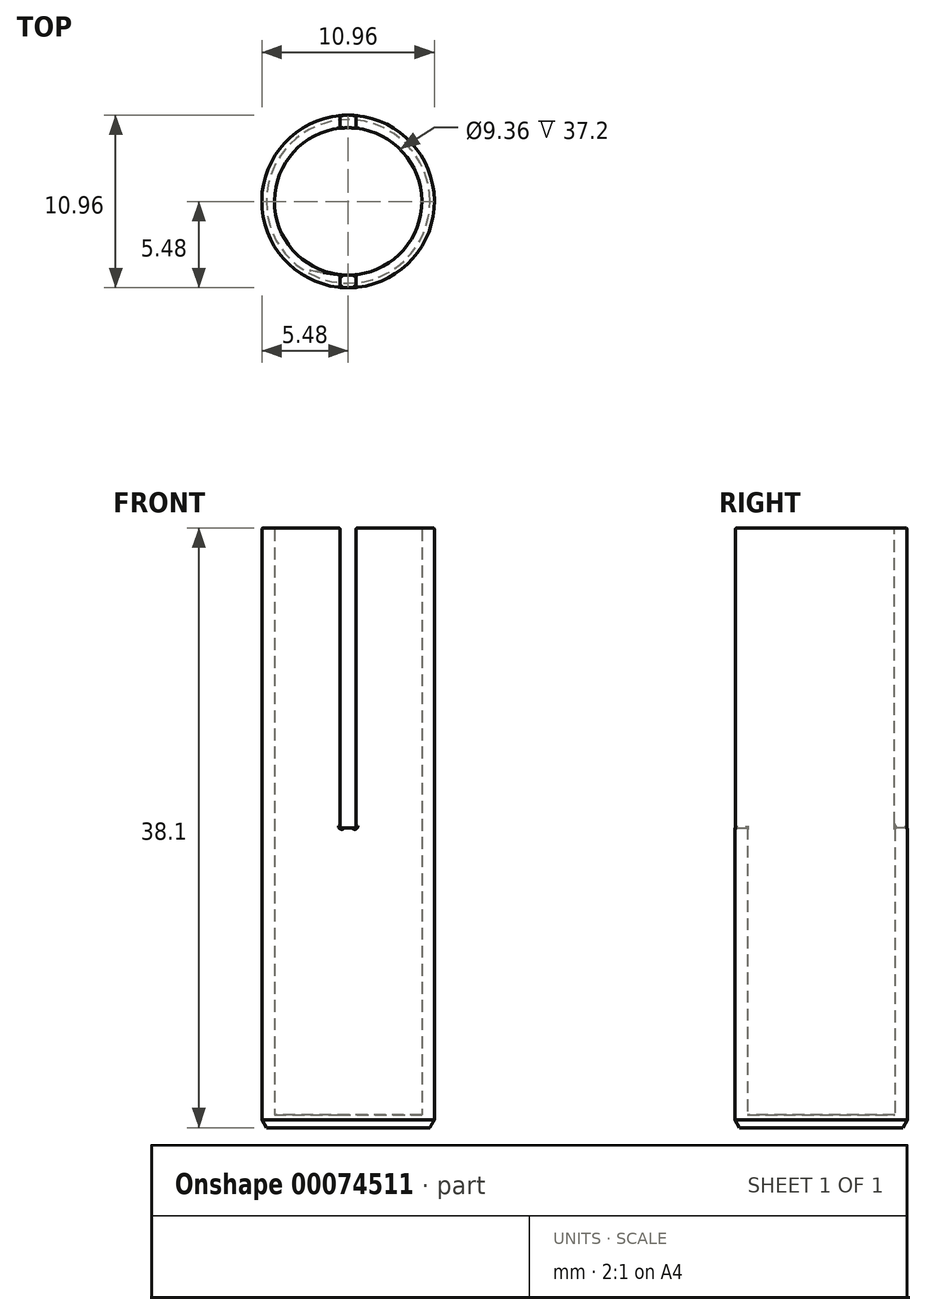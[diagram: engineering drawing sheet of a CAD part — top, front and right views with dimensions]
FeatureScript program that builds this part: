
annotation { "Feature Type Name" : "Feature", "Feature Type Description" : "" }
export const myFeature = defineFeature(function(context is Context, id is Id, definition is map)
    precondition{}
    {
        {
            var Q0;
            Q0=qCreatedBy(makeId("Top.planeOp"),FACE);
            var sketch = newSketch(context, id + "F0", { "sketchPlane" : qUnion([Q0])});
            skCircle(sketch, "E0", {"center": v(0, 0) * mm, "radius": 5.48 * mm});
            skCircle(sketch, "E1", {"center": v(0, 0) * mm, "radius": 5.08 * mm, "construction": true});
            skSolve(sketch);
        }
        {
            var Q0;
            Q0=makeQuery(id+"F0.imprint","IMPRINT",FACE,{"disambiguationData":[TD([[makeQuery(id+"F0.imprint","IMPRINT",EDGE,{"derivedFrom":sQuery(id+"F0.wireOp",EDGE,"E0")}),1.0]])]});
            extrude(context, id + "F1", {"entities" : qUnion([Q0]), "depth" : 38.1 * mm});
        }
        {
            var Q0;
            Q0=makeQuery(id+"F1.opExtrude","CAP_FACE",FACE,{"disambiguationData":[OSD([sQuery(id+"F0.wireOp",EDGE,"E0")])],"isStart":false});
            shell(context, id + "F2", {"entities" : qUnion([Q0]), "thickness" : 0.8 * mm});
        }
        {
            var Q0;
            Q0=makeQuery(id+"F1.opExtrude","CAP_FACE",FACE,{"disambiguationData":[OSD([sQuery(id+"F0.wireOp",EDGE,"E0")])],"isStart":false});
            var sketch = newSketch(context, id + "F3", { "sketchPlane" : qUnion([Q0])});
            skLineSegment(sketch, "E2", {"start": v(0, 5.48) * mm, "end": v(0, 4.68) * mm, "construction": true});
            skLineSegment(sketch, "E3", {"start": v(0.5, 5.46) * mm, "end": v(0.5, 4.65) * mm});
            skLineSegment(sketch, "E4.MirrorCS", {"start": v(-0.5, 5.46) * mm, "end": v(-0.5, 4.65) * mm});
            skArc(sketch, "E5.0", {"start": v(0.5, 4.65) * mm, "mid": v(0, 4.68) * mm, "end": v(-0.5, 4.65) * mm});
            skArc(sketch, "E6.0", {"start": v(0.5, 5.46) * mm, "mid": v(0, 5.48) * mm, "end": v(-0.5, 5.46) * mm});
            skLineSegment(sketch, "E7", {"start": v(0, 4.68) * mm, "end": v(0, -4.68) * mm, "construction": true});
            skLineSegment(sketch, "E8", {"start": v(0, 0) * mm, "end": v(-4.68, 0) * mm, "construction": true});
            skArc(sketch, "E9.MirrorCS", {"start": v(0.5, -4.65) * mm, "mid": v(0, -4.68) * mm, "end": v(-0.5, -4.65) * mm});
            skLineSegment(sketch, "E10.MirrorCS", {"start": v(0.5, -5.46) * mm, "end": v(0.5, -4.65) * mm});
            skArc(sketch, "E11.MirrorCS", {"start": v(0.5, -5.46) * mm, "mid": v(0, -5.48) * mm, "end": v(-0.5, -5.46) * mm});
            skLineSegment(sketch, "E12.MirrorCS", {"start": v(-0.5, -5.46) * mm, "end": v(-0.5, -4.65) * mm});
            skSolve(sketch);
        }
        {
            var Q0;
            Q0 = qSketchRegion(id + "F3", true);
            extrude(context, id + "F4", {"entities" : qUnion([Q0]), "operationType" : NewBodyOperationType.REMOVE, "oppositeDirection" : true, "depth" : 19.05 * mm});
        }
        {
            var Q0;
            {var subQ0=sQuery(id+"F0.wireOp",EDGE,"E0");Q0=makeQuery(id+"F4.boolean.opBoolean","SPLIT",FACE,{"disambiguationData":[TD([makeQuery(id+"F4.opExtrude","SWEPT_FACE",FACE,{"disambiguationData":[OSD([sQuery(id+"F3.wireOp",EDGE,"E4.MirrorCS")])]})])],"derivedFrom":makeQuery(id+"F1.opExtrude","CAP_FACE",FACE,{"disambiguationData":[OSD([subQ0])],"isStart":false})});}
            var Q1;
            {var subQ0=sQuery(id+"F0.wireOp",EDGE,"E0");Q1=makeQuery(id+"F4.boolean.opBoolean","SPLIT",FACE,{"disambiguationData":[TD([makeQuery(id+"F4.opExtrude","SWEPT_FACE",FACE,{"disambiguationData":[OSD([sQuery(id+"F3.wireOp",EDGE,"E3")])]})])],"derivedFrom":makeQuery(id+"F1.opExtrude","CAP_FACE",FACE,{"disambiguationData":[OSD([subQ0])],"isStart":false})});}
            var Q2;
            Q2=makeQuery(id+"F4.boolean.opBoolean","COPY",FACE,{"derivedFrom":makeQuery(id+"F4.opExtrude","SWEPT_FACE",FACE,{"disambiguationData":[OSD([sQuery(id+"F3.wireOp",EDGE,"E10.MirrorCS")])]})});
            var Q3;
            Q3=makeQuery(id+"F4.boolean.opBoolean","COPY",FACE,{"derivedFrom":makeQuery(id+"F4.opExtrude","SWEPT_FACE",FACE,{"disambiguationData":[OSD([sQuery(id+"F3.wireOp",EDGE,"E12.MirrorCS")])]})});
            var Q4;
            Q4=makeQuery(id+"F4.boolean.opBoolean","COPY",FACE,{"derivedFrom":makeQuery(id+"F4.opExtrude","CAP_FACE",FACE,{"disambiguationData":[OSD([sQuery(id+"F3.wireOp",EDGE,"E3"),sQuery(id+"F3.wireOp",EDGE,"E4.MirrorCS"),sQuery(id+"F3.wireOp",EDGE,"E5.0"),sQuery(id+"F3.wireOp",EDGE,"E6.0")])],"isStart":false})});
            fillet(context, id + "F5", {"entities" : qUnion([Q0, Q1, Q2, Q3, Q4]), "radius" : 0.1 * mm, "tangentPropagation" : true, "allowEdgeOverflow" : false});
        }
        {
            var Q0;
            Q0=makeQuery(id+"F1.opExtrude","CAP_EDGE",EDGE,{"disambiguationData":[OSD([sQuery(id+"F0.wireOp",EDGE,"E0")])],"isStart":true});
            chamfer(context, id + "F6", {"entities" : qUnion([Q0]), "chamferType" : ChamferType.OFFSET_ANGLE, "width" : 0.5 * mm, "oppositeDirection" : false, "angle" : 30 * degree, "tangentPropagation" : true});
        }
    });
